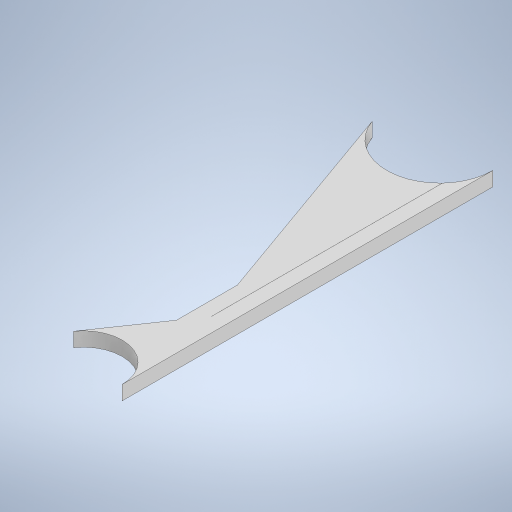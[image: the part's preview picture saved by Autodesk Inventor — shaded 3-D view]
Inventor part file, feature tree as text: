
AUTODESK INVENTOR PART (.ipt)
format: ipt  version: 2024 (Build 280153000, 153)  size: 245,248 bytes
history: native  units: mm
features: extrude x1, sketch x1
ambient origin geometry x8: Origin, YZ Plane, XZ Plane, XY Plane, X Axis, Y Axis, Z Axis, Center Point
bodies: Solid1 (feature_tree)
feature tree (2):
  extrude  "Extrusion1"  Depth=20.0mm
  sketch  "Sketch1"  dims[d0=450.0mm d1=200.0mm d2=160.0mm d3=20.0mm d4=20.0mm d5=20.0mm d6=0.0mm]
